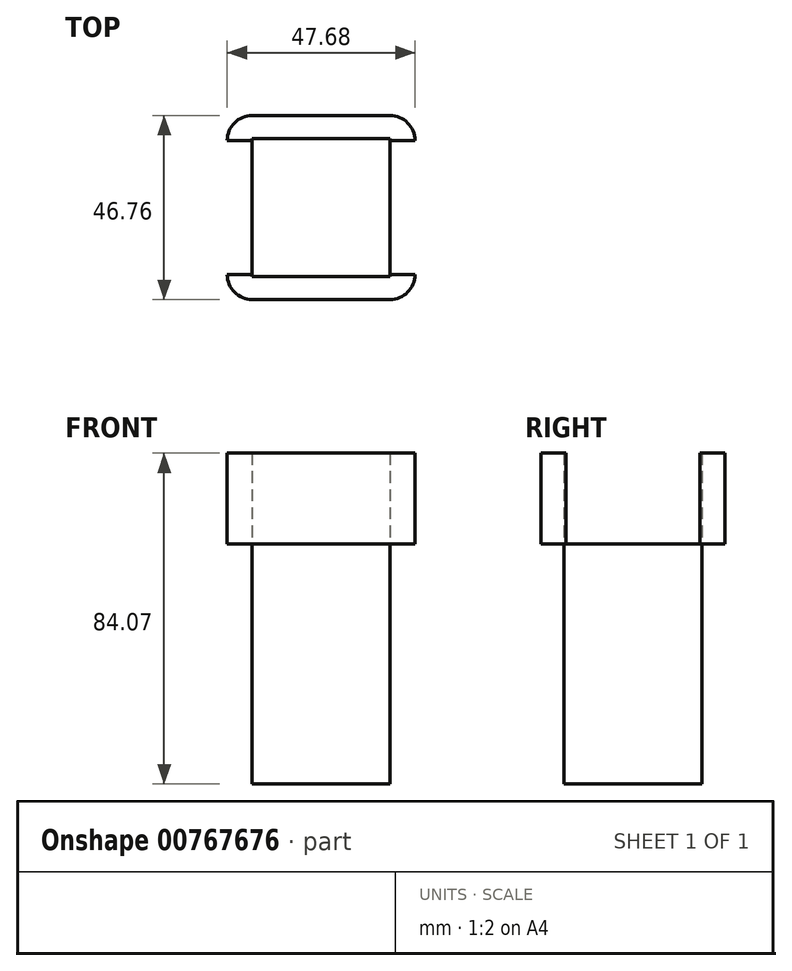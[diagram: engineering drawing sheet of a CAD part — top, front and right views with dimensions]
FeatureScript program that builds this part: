
annotation { "Feature Type Name" : "Feature", "Feature Type Description" : "" }
export const myFeature = defineFeature(function(context is Context, id is Id, definition is map)
    precondition{}
    {
        {
            var Q0;
            Q0=qCreatedBy(makeId("Top.planeOp"),FACE);
            var sketch = newSketch(context, id + "F0", { "sketchPlane" : qUnion([Q0])});
            skLineSegment(sketch, "E0.bottom", {"start": v(17.5, 17.5) * mm, "end": v(-17.5, 17.5) * mm});
            skLineSegment(sketch, "E0.top", {"start": v(17.5, -17.5) * mm, "end": v(-17.5, -17.5) * mm});
            skLineSegment(sketch, "E0.left", {"start": v(17.5, 17.5) * mm, "end": v(17.5, -17.5) * mm});
            skLineSegment(sketch, "E0.right", {"start": v(-17.5, 17.5) * mm, "end": v(-17.5, -17.5) * mm});
            skPoint(sketch, "E0.middle", {"position": v(0, 0) * mm});
            skSolve(sketch);
        }
        {
            var Q0;
            Q0=makeQuery(id+"F0.imprint","IMPRINT",FACE,{"disambiguationData":[TD([[makeQuery(id+"F0.imprint","IMPRINT",EDGE,{"derivedFrom":sQuery(id+"F0.wireOp",EDGE,"E0.bottom")}),1.0]])]});
            extrude(context, id + "F1", {"entities" : qUnion([Q0]), "depth" : 60.96 * mm, "offsetDistance" : 25.4 * mm});
        }
        {
            var Q0;
            Q0=makeQuery(id+"F1.opExtrude","CAP_FACE",FACE,{"disambiguationData":[OSD([sQuery(id+"F0.wireOp",EDGE,"E0.bottom"),sQuery(id+"F0.wireOp",EDGE,"E0.top"),sQuery(id+"F0.wireOp",EDGE,"E0.left"),sQuery(id+"F0.wireOp",EDGE,"E0.right")])],"isStart":false});
            var sketch = newSketch(context, id + "F2", { "sketchPlane" : qUnion([Q0])});
            skLineSegment(sketch, "E1.bottom", {"start": v(-17.5, 23.38) * mm, "end": v(17.5, 23.38) * mm});
            skLineSegment(sketch, "E1.top", {"start": v(-17.5, -23.38) * mm, "end": v(17.5, -23.38) * mm});
            skLineSegment(sketch, "E1.left", {"start": v(-23.84, 17.03) * mm, "end": v(-23.84, -17.03) * mm});
            skLineSegment(sketch, "E1.right", {"start": v(23.84, 17.03) * mm, "end": v(23.84, -17.03) * mm});
            skPoint(sketch, "E1.middle", {"position": v(0, 0) * mm});
            skPoint(sketch, "E2.visualSharp", {"position": v(-23.84, 23.38) * mm});
            skArc(sketch, "E2.filletArc", {"start": v(-17.5, 23.38) * mm, "mid": v(-21.98, 21.52) * mm, "end": v(-23.84, 17.03) * mm});
            skPoint(sketch, "E3.visualSharp", {"position": v(23.84, 23.38) * mm});
            skArc(sketch, "E3.filletArc", {"start": v(23.84, 17.03) * mm, "mid": v(21.98, 21.52) * mm, "end": v(17.5, 23.38) * mm});
            skPoint(sketch, "E4.visualSharp", {"position": v(-23.84, -23.38) * mm});
            skArc(sketch, "E4.filletArc", {"start": v(-23.84, -17.03) * mm, "mid": v(-21.98, -21.52) * mm, "end": v(-17.5, -23.38) * mm});
            skPoint(sketch, "E5.visualSharp", {"position": v(23.84, -23.38) * mm});
            skArc(sketch, "E5.filletArc", {"start": v(17.5, -23.38) * mm, "mid": v(21.98, -21.52) * mm, "end": v(23.84, -17.03) * mm});
            skSolve(sketch);
        }
        {
            var Q0;
            Q0=makeQuery(id+"F2.imprint","IMPRINT",FACE,{"disambiguationData":[TD([[makeQuery(id+"F2.imprint","IMPRINT",EDGE,{"derivedFrom":sQuery(id+"F2.wireOp",EDGE,"E1.bottom")}),-1.0]])]});
            extrude(context, id + "F3", {"entities" : qUnion([Q0]), "depth" : 23.1 * mm, "offsetDistance" : 25.4 * mm});
        }
        {
            var Q0;
            Q0=makeQuery(id+"F3.opExtrude","SWEPT_FACE",FACE,{"disambiguationData":[OSD([sQuery(id+"F2.wireOp",EDGE,"E1.right")])]});
            extrude(context, id + "F4", {"entities" : qUnion([Q0]), "operationType" : NewBodyOperationType.REMOVE, "oppositeDirection" : true, "depth" : 64.52 * mm, "offsetDistance" : 25.4 * mm});
        }
    });
